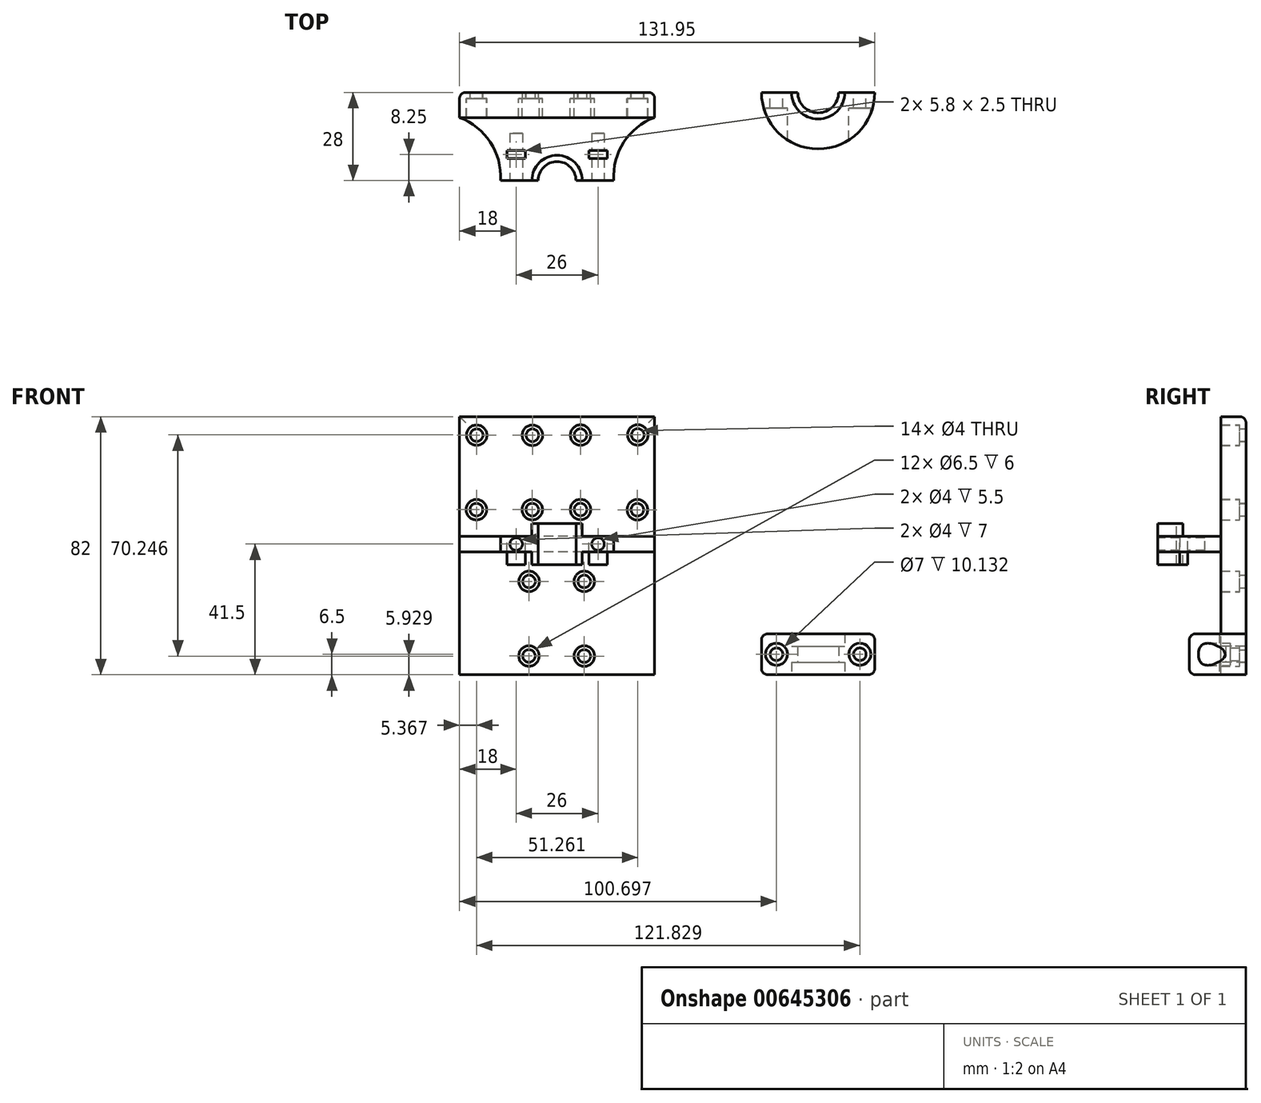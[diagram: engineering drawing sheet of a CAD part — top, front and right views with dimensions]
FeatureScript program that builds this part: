
annotation { "Feature Type Name" : "Feature", "Feature Type Description" : "" }
export const myFeature = defineFeature(function(context is Context, id is Id, definition is map)
    precondition{}
    {
        {
            var Q0;
            Q0=qCreatedBy(makeId("Front.planeOp"),FACE);
            var sketch = newSketch(context, id + "F0", { "sketchPlane" : qUnion([Q0])});
            skLineSegment(sketch, "E0.bottom", {"start": v(0, 0) * mm, "end": v(-62, 0) * mm});
            skLineSegment(sketch, "E0.top", {"start": v(0, 82) * mm, "end": v(-62, 82) * mm});
            skLineSegment(sketch, "E0.left", {"start": v(0, 0) * mm, "end": v(0, 82) * mm});
            skLineSegment(sketch, "E0.right", {"start": v(-62, 0) * mm, "end": v(-62, 82) * mm});
            skLineSegment(sketch, "E1.bottom", {"start": v(-62, 82) * mm, "end": v(-32, 82) * mm});
            skLineSegment(sketch, "E1.top", {"start": v(-62, 48) * mm, "end": v(-32, 48) * mm});
            skLineSegment(sketch, "E1.left", {"start": v(-62, 82) * mm, "end": v(-62, 48) * mm});
            skLineSegment(sketch, "E1.right", {"start": v(-32, 82) * mm, "end": v(-32, 48) * mm});
            skLineSegment(sketch, "E2.bottom", {"start": v(0, 82) * mm, "end": v(-30, 82) * mm});
            skLineSegment(sketch, "E2.top", {"start": v(0, 48) * mm, "end": v(-30, 48) * mm});
            skLineSegment(sketch, "E2.left", {"start": v(0, 82) * mm, "end": v(0, 48) * mm});
            skLineSegment(sketch, "E2.right", {"start": v(-30, 82) * mm, "end": v(-30, 48) * mm});
            skLineSegment(sketch, "E3", {"start": v(-62, 0) * mm, "end": v(-46, 0) * mm});
            skLineSegment(sketch, "E4.bottom", {"start": v(-46, 0) * mm, "end": v(-16, 0) * mm});
            skLineSegment(sketch, "E4.top", {"start": v(-46, 34) * mm, "end": v(-16, 34) * mm});
            skLineSegment(sketch, "E4.left", {"start": v(-46, 0) * mm, "end": v(-46, 34) * mm});
            skLineSegment(sketch, "E4.right", {"start": v(-16, 0) * mm, "end": v(-16, 34) * mm});
            skLineSegment(sketch, "E5", {"start": v(-62, 82) * mm, "end": v(-58.7, 82) * mm});
            skLineSegment(sketch, "E6", {"start": v(-58.7, 82) * mm, "end": v(-36.7, 82) * mm});
            skLineSegment(sketch, "E7", {"start": v(0, 82) * mm, "end": v(-3.3, 82) * mm});
            skLineSegment(sketch, "E8", {"start": v(-3.3, 82) * mm, "end": v(-25.3, 82) * mm});
            skLineSegment(sketch, "E9", {"start": v(0, 82) * mm, "end": v(0, 78.3) * mm});
            skLineSegment(sketch, "E10", {"start": v(0, 78.3) * mm, "end": v(0, 50.3) * mm});
            skLineSegment(sketch, "E11", {"start": v(-58.7, 82) * mm, "end": v(-58.7, 48) * mm, "construction": true});
            skLineSegment(sketch, "E12", {"start": v(-36.7, 82) * mm, "end": v(-36.7, 48) * mm, "construction": true});
            skLineSegment(sketch, "E13", {"start": v(-25.3, 82) * mm, "end": v(-25.3, 48) * mm, "construction": true});
            skLineSegment(sketch, "E14", {"start": v(-3.3, 82) * mm, "end": v(-3.3, 48) * mm, "construction": true});
            skLineSegment(sketch, "E15", {"start": v(0, 78.3) * mm, "end": v(-58.7, 78.3) * mm, "construction": true});
            skLineSegment(sketch, "E16", {"start": v(0, 50.3) * mm, "end": v(-58.7, 50.3) * mm, "construction": true});
            skLineSegment(sketch, "E17", {"start": v(-62, 0) * mm, "end": v(-42, 0) * mm});
            skLineSegment(sketch, "E18", {"start": v(-42, 0) * mm, "end": v(-20.3, 0) * mm});
            skLineSegment(sketch, "E19", {"start": v(-20.3, 0) * mm, "end": v(0, 0) * mm});
            skLineSegment(sketch, "E20", {"start": v(-42, 0) * mm, "end": v(-42, 34) * mm, "construction": true});
            skLineSegment(sketch, "E21", {"start": v(-20.3, 0) * mm, "end": v(-20.3, 34) * mm, "construction": true});
            skLineSegment(sketch, "E22", {"start": v(-16, 0) * mm, "end": v(-16, 3.9) * mm});
            skLineSegment(sketch, "E23", {"start": v(-16, 3.9) * mm, "end": v(-16, 31.7) * mm});
            skLineSegment(sketch, "E24", {"start": v(-16, 31.7) * mm, "end": v(-42, 31.7) * mm, "construction": true});
            skLineSegment(sketch, "E25", {"start": v(-16, 3.9) * mm, "end": v(-42, 3.9) * mm, "construction": true});
            skCircle(sketch, "E26", {"center": v(-39.91, 29.63) * mm, "radius": 2 * mm});
            skCircle(sketch, "E27", {"center": v(-22.37, 29.64) * mm, "radius": 2 * mm});
            skCircle(sketch, "E28", {"center": v(-22.36, 5.93) * mm, "radius": 2 * mm});
            skCircle(sketch, "E29", {"center": v(-39.93, 5.95) * mm, "radius": 2 * mm});
            skCircle(sketch, "E30", {"center": v(-39.91, 29.63) * mm, "radius": 3.25 * mm});
            skCircle(sketch, "E31", {"center": v(-22.37, 29.64) * mm, "radius": 3.25 * mm});
            skCircle(sketch, "E32", {"center": v(-39.93, 5.95) * mm, "radius": 3.25 * mm});
            skCircle(sketch, "E33", {"center": v(-22.36, 5.93) * mm, "radius": 3.25 * mm});
            skCircle(sketch, "E34", {"center": v(-56.63, 52.43) * mm, "radius": 2 * mm});
            skCircle(sketch, "E35", {"center": v(-38.89, 52.44) * mm, "radius": 2 * mm});
            skCircle(sketch, "E36", {"center": v(-56.55, 76.1) * mm, "radius": 2 * mm});
            skCircle(sketch, "E37", {"center": v(-38.84, 76.08) * mm, "radius": 2 * mm});
            skCircle(sketch, "E38", {"center": v(-23.55, 76.11) * mm, "radius": 2 * mm});
            skCircle(sketch, "E39", {"center": v(-5.37, 76.17) * mm, "radius": 2 * mm});
            skCircle(sketch, "E40", {"center": v(-5.5, 52.4) * mm, "radius": 2 * mm});
            skCircle(sketch, "E41", {"center": v(-23.55, 52.48) * mm, "radius": 2 * mm});
            skCircle(sketch, "E42", {"center": v(-56.55, 76.1) * mm, "radius": 3.25 * mm});
            skCircle(sketch, "E43", {"center": v(-38.84, 76.08) * mm, "radius": 3.25 * mm});
            skCircle(sketch, "E44", {"center": v(-56.63, 52.43) * mm, "radius": 3.25 * mm});
            skCircle(sketch, "E45", {"center": v(-38.89, 52.44) * mm, "radius": 3.25 * mm});
            skCircle(sketch, "E46", {"center": v(-23.55, 52.48) * mm, "radius": 3.25 * mm});
            skCircle(sketch, "E47", {"center": v(-5.5, 52.4) * mm, "radius": 3.25 * mm});
            skCircle(sketch, "E48", {"center": v(-23.55, 76.11) * mm, "radius": 3.25 * mm});
            skCircle(sketch, "E49", {"center": v(-5.37, 76.17) * mm, "radius": 3.25 * mm});
            skSolve(sketch);
        }
        {
            var Q0;
            Q0 = qSketchRegion(id + "F0", true);
            extrude(context, id + "F1", {"entities" : qUnion([Q0]), "depth" : 8 * mm, "offsetDistance" : 25 * mm});
        }
        {
            var Q0;
            Q0=makeQuery(id+"F0.imprint","IMPRINT",FACE,{"disambiguationData":[TD([[makeQuery(id+"F0.imprint","IMPRINT",EDGE,{"derivedFrom":sQuery(id+"F0.wireOp",EDGE,"E36")}),-1.0]])]});
            var Q1;
            Q1=makeQuery(id+"F0.imprint","IMPRINT",FACE,{"disambiguationData":[TD([[makeQuery(id+"F0.imprint","IMPRINT",EDGE,{"derivedFrom":sQuery(id+"F0.wireOp",EDGE,"E37")}),-1.0]])]});
            var Q2;
            Q2=makeQuery(id+"F0.imprint","IMPRINT",FACE,{"disambiguationData":[TD([[makeQuery(id+"F0.imprint","IMPRINT",EDGE,{"derivedFrom":sQuery(id+"F0.wireOp",EDGE,"E38")}),-1.0]])]});
            var Q3;
            Q3=makeQuery(id+"F0.imprint","IMPRINT",FACE,{"disambiguationData":[TD([[makeQuery(id+"F0.imprint","IMPRINT",EDGE,{"derivedFrom":sQuery(id+"F0.wireOp",EDGE,"E39")}),-1.0]])]});
            var Q4;
            Q4=makeQuery(id+"F0.imprint","IMPRINT",FACE,{"disambiguationData":[TD([[makeQuery(id+"F0.imprint","IMPRINT",EDGE,{"derivedFrom":sQuery(id+"F0.wireOp",EDGE,"E40")}),-1.0]])]});
            var Q5;
            Q5=makeQuery(id+"F0.imprint","IMPRINT",FACE,{"disambiguationData":[TD([[makeQuery(id+"F0.imprint","IMPRINT",EDGE,{"derivedFrom":sQuery(id+"F0.wireOp",EDGE,"E41")}),-1.0]])]});
            var Q6;
            Q6=makeQuery(id+"F0.imprint","IMPRINT",FACE,{"disambiguationData":[TD([[makeQuery(id+"F0.imprint","IMPRINT",EDGE,{"derivedFrom":sQuery(id+"F0.wireOp",EDGE,"E35")}),-1.0]])]});
            var Q7;
            Q7=makeQuery(id+"F0.imprint","IMPRINT",FACE,{"disambiguationData":[TD([[makeQuery(id+"F0.imprint","IMPRINT",EDGE,{"derivedFrom":sQuery(id+"F0.wireOp",EDGE,"E34")}),-1.0]])]});
            var Q8;
            Q8=makeQuery(id+"F0.imprint","IMPRINT",FACE,{"disambiguationData":[TD([[makeQuery(id+"F0.imprint","IMPRINT",EDGE,{"derivedFrom":sQuery(id+"F0.wireOp",EDGE,"E26")}),-1.0]])]});
            var Q9;
            Q9=makeQuery(id+"F0.imprint","IMPRINT",FACE,{"disambiguationData":[TD([[makeQuery(id+"F0.imprint","IMPRINT",EDGE,{"derivedFrom":sQuery(id+"F0.wireOp",EDGE,"E27")}),-1.0]])]});
            var Q10;
            Q10=makeQuery(id+"F0.imprint","IMPRINT",FACE,{"disambiguationData":[TD([[makeQuery(id+"F0.imprint","IMPRINT",EDGE,{"derivedFrom":sQuery(id+"F0.wireOp",EDGE,"E28")}),-1.0]])]});
            var Q11;
            Q11=makeQuery(id+"F0.imprint","IMPRINT",FACE,{"disambiguationData":[TD([[makeQuery(id+"F0.imprint","IMPRINT",EDGE,{"derivedFrom":sQuery(id+"F0.wireOp",EDGE,"E29")}),-1.0]])]});
            extrude(context, id + "F2", {"entities" : qUnion([Q0, Q1, Q2, Q3, Q4, Q5, Q6, Q7, Q8, Q9, Q10, Q11]), "operationType" : NewBodyOperationType.ADD, "depth" : 2 * mm, "offsetDistance" : 25 * mm});
        }
        {
            var Q0;
            Q0=makeQuery(id+"F1.opExtrude","CAP_FACE",FACE,{"disambiguationData":[OSD([sQuery(id+"F0.wireOp",EDGE,"E0.top"),sQuery(id+"F0.wireOp",EDGE,"E0.left"),sQuery(id+"F0.wireOp",EDGE,"E0.right"),sQuery(id+"F0.wireOp",EDGE,"E1.bottom"),sQuery(id+"F0.wireOp",EDGE,"E1.left"),sQuery(id+"F0.wireOp",EDGE,"E2.bottom"),sQuery(id+"F0.wireOp",EDGE,"E2.left"),sQuery(id+"F0.wireOp",EDGE,"E5"),sQuery(id+"F0.wireOp",EDGE,"E6"),sQuery(id+"F0.wireOp",EDGE,"E7"),sQuery(id+"F0.wireOp",EDGE,"E8"),sQuery(id+"F0.wireOp",EDGE,"E9"),sQuery(id+"F0.wireOp",EDGE,"E10"),sQuery(id+"F0.wireOp",EDGE,"E17"),sQuery(id+"F0.wireOp",EDGE,"E18"),sQuery(id+"F0.wireOp",EDGE,"E19"),sQuery(id+"F0.wireOp",EDGE,"E30"),sQuery(id+"F0.wireOp",EDGE,"E31"),sQuery(id+"F0.wireOp",EDGE,"E32"),sQuery(id+"F0.wireOp",EDGE,"E33"),sQuery(id+"F0.wireOp",EDGE,"E42"),sQuery(id+"F0.wireOp",EDGE,"E43"),sQuery(id+"F0.wireOp",EDGE,"E44"),sQuery(id+"F0.wireOp",EDGE,"E45"),sQuery(id+"F0.wireOp",EDGE,"E46"),sQuery(id+"F0.wireOp",EDGE,"E47"),sQuery(id+"F0.wireOp",EDGE,"E48"),sQuery(id+"F0.wireOp",EDGE,"E49")])],"isStart":false});
            var sketch = newSketch(context, id + "F3", { "sketchPlane" : qUnion([Q0])});
            skLineSegment(sketch, "E50", {"start": v(0, 0) * mm, "end": v(0, 48) * mm});
            skLineSegment(sketch, "E51", {"start": v(0, 48) * mm, "end": v(-62, 48) * mm});
            skLineSegment(sketch, "E52", {"start": v(0, 48) * mm, "end": v(0, 35) * mm});
            skLineSegment(sketch, "E53", {"start": v(0, 35) * mm, "end": v(-62, 35) * mm});
            skLineSegment(sketch, "E54", {"start": v(-62, 35) * mm, "end": v(-62, 48) * mm});
            skSolve(sketch);
        }
        {
            var Q0;
            Q0 = qSketchRegion(id + "F3", true);
            extrude(context, id + "F4", {"entities" : qUnion([Q0]), "operationType" : NewBodyOperationType.ADD, "depth" : 20 * mm, "offsetDistance" : 25 * mm});
        }
        {
            var Q0;
            Q0=makeQuery(id+"F4.opExtrude","SWEPT_FACE",FACE,{"disambiguationData":[OSD([sQuery(id+"F3.wireOp",EDGE,"E51")])]});
            var sketch = newSketch(context, id + "F5", { "sketchPlane" : qUnion([Q0])});
            skLineSegment(sketch, "E55", {"start": v(-62, -28) * mm, "end": v(-39, -28) * mm});
            skLineSegment(sketch, "E56", {"start": v(-39, -28) * mm, "end": v(-23, -28) * mm});
            skLineSegment(sketch, "E57", {"start": v(-39, -28) * mm, "end": v(-49, -28) * mm});
            skLineSegment(sketch, "E58", {"start": v(-23, -28) * mm, "end": v(-13, -28) * mm});
            skArc(sketch, "E59", {"start": v(-49, -28) * mm, "mid": v(-52.2, -15.85) * mm, "end": v(-62, -8) * mm});
            skArc(sketch, "E60", {"start": v(0, -8) * mm, "mid": v(-9.8, -15.85) * mm, "end": v(-13, -28) * mm});
            skArc(sketch, "E61", {"start": v(-39, -28) * mm, "mid": v(-31, -20) * mm, "end": v(-23, -28) * mm});
            skArc(sketch, "E62", {"start": v(-25, -28) * mm, "mid": v(-31, -22) * mm, "end": v(-37, -28) * mm});
            skLineSegment(sketch, "E63", {"start": v(-49, -28) * mm, "end": v(-46.9, -28) * mm});
            skLineSegment(sketch, "E64", {"start": v(-46.9, -21) * mm, "end": v(-46.9, -18.5) * mm});
            skLineSegment(sketch, "E65", {"start": v(-46.9, -18.5) * mm, "end": v(-41.1, -18.5) * mm});
            skLineSegment(sketch, "E66", {"start": v(-41.1, -18.5) * mm, "end": v(-41.1, -21) * mm});
            skLineSegment(sketch, "E67", {"start": v(-41.1, -21) * mm, "end": v(-46.9, -21) * mm});
            skLineSegment(sketch, "E68", {"start": v(-31, -28) * mm, "end": v(-31, -15.15) * mm, "construction": true});
            skLineSegment(sketch, "E69.MirrorCS", {"start": v(-20.9, -18.5) * mm, "end": v(-20.9, -21) * mm});
            skLineSegment(sketch, "E70.MirrorCS", {"start": v(-15.1, -18.5) * mm, "end": v(-20.9, -18.5) * mm});
            skLineSegment(sketch, "E71.MirrorCS", {"start": v(-15.1, -21) * mm, "end": v(-15.1, -18.5) * mm});
            skLineSegment(sketch, "E72.MirrorCS", {"start": v(-20.9, -21) * mm, "end": v(-15.1, -21) * mm});
            skSolve(sketch);
        }
        {
            var Q0;
            Q0=makeQuery(id+"F5.imprint","IMPRINT",FACE,{"disambiguationData":[TD([[makeQuery(id+"F5.imprint","IMPRINT",EDGE,{"derivedFrom":sQuery(id+"F5.wireOp",EDGE,"E55")}),-1.0]])]});
            var Q1;
            {var subQ0=sQuery(id+"F5.wireOp",EDGE,"E60");Q1=makeQuery(id+"F5.imprint","IMPRINT",FACE,{"disambiguationData":[TD([[makeQuery(id+"F5.imprint","IMPRINT",EDGE,{"derivedFrom":subQ0}),1.0]])]});}
            extrude(context, id + "F6", {"entities" : qUnion([Q0, Q1]), "operationType" : NewBodyOperationType.REMOVE, "oppositeDirection" : true, "depth" : 25 * mm, "offsetDistance" : 25 * mm});
        }
        {
            var Q0;
            Q0=makeQuery(id+"F5.imprint","IMPRINT",FACE,{"disambiguationData":[TD([[makeQuery(id+"F5.imprint","IMPRINT",EDGE,{"derivedFrom":sQuery(id+"F5.wireOp",EDGE,"E65")}),-1.0]])]});
            var Q1;
            Q1=makeQuery(id+"F5.imprint","IMPRINT",FACE,{"disambiguationData":[TD([[makeQuery(id+"F5.imprint","IMPRINT",EDGE,{"derivedFrom":sQuery(id+"F5.wireOp",EDGE,"66e045d4-452c-4d9e-82fe-42991698a6ae0.MirrorCS")}),1.0]])]});
            extrude(context, id + "F7", {"entities" : qUnion([Q0, Q1]), "operationType" : NewBodyOperationType.REMOVE, "oppositeDirection" : true, "depth" : 9 * mm, "offsetDistance" : 25 * mm});
        }
        {
            var Q0;
            {var subQ0=sQuery(id+"F5.wireOp",EDGE,"E62");Q0=makeQuery(id+"F5.imprint","IMPRINT",FACE,{"disambiguationData":[TD([[makeQuery(id+"F5.imprint","IMPRINT",EDGE,{"derivedFrom":subQ0}),1.0]])]});}
            var Q1;
            {var subQ0=sQuery(id+"F5.wireOp",EDGE,"E61");Q1=makeQuery(id+"F5.imprint","IMPRINT",FACE,{"disambiguationData":[TD([[makeQuery(id+"F5.imprint","IMPRINT",EDGE,{"derivedFrom":subQ0}),-1.0]])]});}
            extrude(context, id + "F8", {"entities" : qUnion([Q0, Q1]), "operationType" : NewBodyOperationType.REMOVE, "oppositeDirection" : true, "depth" : 25 * mm, "offsetDistance" : 25 * mm});
        }
        {
            var Q0;
            {var subQ0=sQuery(id+"F5.wireOp",EDGE,"E61");Q0=makeQuery(id+"F5.imprint","IMPRINT",FACE,{"disambiguationData":[TD([[makeQuery(id+"F5.imprint","IMPRINT",EDGE,{"derivedFrom":subQ0}),-1.0]])]});}
            extrude(context, id + "F9", {"entities" : qUnion([Q0]), "operationType" : NewBodyOperationType.ADD, "oppositeDirection" : true, "depth" : 9 * mm, "offsetDistance" : 25 * mm});
        }
        {
            var Q0;
            {var subQ0=sQuery(id+"F5.wireOp",EDGE,"E61");Q0=makeQuery(id+"F5.imprint","IMPRINT",FACE,{"disambiguationData":[TD([[makeQuery(id+"F5.imprint","IMPRINT",EDGE,{"derivedFrom":subQ0}),-1.0]])]});}
            extrude(context, id + "F10", {"entities" : qUnion([Q0]), "operationType" : NewBodyOperationType.REMOVE, "oppositeDirection" : true, "depth" : 4 * mm, "offsetDistance" : 25 * mm});
        }
        {
            var Q0;
            {var subQ1=sQuery(id+"F5.wireOp",EDGE,"E56");var subQ2=sQuery(id+"F3.wireOp",EDGE,"E51");var subQ3=sQuery(id+"F3.wireOp",EDGE,"E53");Q0=makeQuery(id+"F9.boolean.opBoolean","MERGE",FACE,{"derivedFrom":[makeQuery(id+"F8.boolean.opBoolean","SPLIT",FACE,{"disambiguationData":[TD([makeQuery(id+"F6.boolean.opBoolean","COPY",FACE,{"derivedFrom":makeQuery(id+"F6.opExtrude","SWEPT_FACE",FACE,{"disambiguationData":[OSD([sQuery(id+"F5.wireOp",EDGE,"E59")])]})})])],"derivedFrom":makeQuery(id+"F4.opExtrude","CAP_FACE",FACE,{"disambiguationData":[OSD([subQ2,sQuery(id+"F3.wireOp",EDGE,"E52"),subQ3,sQuery(id+"F3.wireOp",EDGE,"E54")])],"isStart":false})}),makeQuery(id+"F9.opExtrude","SWEPT_FACE",FACE,{"disambiguationData":[OSD([subQ1]),TDD([makeQuery(id+"F5.imprint","IMPRINT",EDGE,{"disambiguationData":[TD([[makeQuery(id+"F5.imprint","INTERSECT",VERTEX,{"disambiguationData":[OD(1.0)],"derivedFrom":[subQ1,sQuery(id+"F5.wireOp",EDGE,"E62")]}),-1.0]])],"derivedFrom":subQ1})])]})]});}
            var sketch = newSketch(context, id + "F11", { "sketchPlane" : qUnion([Q0])});
            skLineSegment(sketch, "E73", {"start": v(-49, 48) * mm, "end": v(-44, 48) * mm});
            skLineSegment(sketch, "E74", {"start": v(-44, 48) * mm, "end": v(-44, 41.5) * mm});
            skPoint(sketch, "E74.endSnap0", {"position": v(-49, 41.5) * mm});
            skCircle(sketch, "E75", {"center": v(-44, 41.5) * mm, "radius": 2 * mm});
            skSolve(sketch);
        }
        {
            var Q0;
            Q0 = qSketchRegion(id + "F11", true);
            extrude(context, id + "F12", {"entities" : qUnion([Q0]), "operationType" : NewBodyOperationType.REMOVE, "oppositeDirection" : true, "depth" : 15 * mm, "offsetDistance" : 25 * mm});
        }
        {
            var Q0;
            {var subQ1=sQuery(id+"F5.wireOp",EDGE,"E56");var subQ2=sQuery(id+"F3.wireOp",EDGE,"E51");var subQ3=sQuery(id+"F3.wireOp",EDGE,"E53");Q0=makeQuery(id+"F9.boolean.opBoolean","MERGE",FACE,{"derivedFrom":[makeQuery(id+"F8.boolean.opBoolean","SPLIT",FACE,{"disambiguationData":[TD([makeQuery(id+"F6.boolean.opBoolean","COPY",FACE,{"derivedFrom":makeQuery(id+"F6.opExtrude","SWEPT_FACE",FACE,{"disambiguationData":[OSD([sQuery(id+"F5.wireOp",EDGE,"E60")])]})})])],"derivedFrom":makeQuery(id+"F4.opExtrude","CAP_FACE",FACE,{"disambiguationData":[OSD([subQ2,sQuery(id+"F3.wireOp",EDGE,"E52"),subQ3,sQuery(id+"F3.wireOp",EDGE,"E54")])],"isStart":false})}),makeQuery(id+"F9.opExtrude","SWEPT_FACE",FACE,{"disambiguationData":[OSD([subQ1]),TDD([makeQuery(id+"F5.imprint","IMPRINT",EDGE,{"disambiguationData":[TD([[makeQuery(id+"F5.imprint","INTERSECT",VERTEX,{"disambiguationData":[OD(0.0)],"derivedFrom":[subQ1,sQuery(id+"F5.wireOp",EDGE,"E62")]}),1.0]])],"derivedFrom":subQ1})])]})]});}
            var sketch = newSketch(context, id + "F13", { "sketchPlane" : qUnion([Q0])});
            skLineSegment(sketch, "E76", {"start": v(-13, 48) * mm, "end": v(-18, 48) * mm});
            skLineSegment(sketch, "E77", {"start": v(-18, 48) * mm, "end": v(-18, 41.5) * mm});
            skPoint(sketch, "E77.endSnap0", {"position": v(-13, 41.5) * mm});
            skCircle(sketch, "E78", {"center": v(-18, 41.5) * mm, "radius": 2 * mm});
            skSolve(sketch);
        }
        {
            var Q0;
            Q0 = qSketchRegion(id + "F13", true);
            extrude(context, id + "F14", {"entities" : qUnion([Q0]), "operationType" : NewBodyOperationType.REMOVE, "oppositeDirection" : true, "depth" : 15 * mm, "offsetDistance" : 25 * mm});
        }
        {
            var Q0;
            Q0=makeQuery(id+"F1.opExtrude","CAP_EDGE",EDGE,{"disambiguationData":[OSD([sQuery(id+"F0.wireOp",EDGE,"E0.top"),sQuery(id+"F0.wireOp",EDGE,"E1.bottom"),sQuery(id+"F0.wireOp",EDGE,"E2.bottom"),sQuery(id+"F0.wireOp",EDGE,"E5"),sQuery(id+"F0.wireOp",EDGE,"E6"),sQuery(id+"F0.wireOp",EDGE,"E7"),sQuery(id+"F0.wireOp",EDGE,"E8")])],"isStart":true});
            var Q1;
            Q1=makeQuery(id+"F1.opExtrude","CAP_EDGE",EDGE,{"disambiguationData":[OSD([sQuery(id+"F0.wireOp",EDGE,"E0.right"),sQuery(id+"F0.wireOp",EDGE,"E1.left")])],"isStart":true});
            var Q2;
            Q2=makeQuery(id+"F1.opExtrude","CAP_EDGE",EDGE,{"disambiguationData":[OSD([sQuery(id+"F0.wireOp",EDGE,"E0.left"),sQuery(id+"F0.wireOp",EDGE,"E2.left"),sQuery(id+"F0.wireOp",EDGE,"E9"),sQuery(id+"F0.wireOp",EDGE,"E10")])],"isStart":true});
            var Q3;
            Q3=makeQuery(id+"F1.opExtrude","CAP_EDGE",EDGE,{"disambiguationData":[OSD([sQuery(id+"F0.wireOp",EDGE,"E17"),sQuery(id+"F0.wireOp",EDGE,"E18"),sQuery(id+"F0.wireOp",EDGE,"E19")])],"isStart":true});
            var Q4;
            Q4=makeQuery(id+"F6.boolean.opBoolean","COPY",EDGE,{"derivedFrom":makeQuery(id+"F6.opExtrude","CAP_EDGE",EDGE,{"disambiguationData":[OSD([sQuery(id+"F5.wireOp",EDGE,"E60")])],"isStart":true})});
            var Q5;
            Q5=makeQuery(id+"F6.boolean.opBoolean","INTERSECT",EDGE,{"derivedFrom":[makeQuery(id+"F4.opExtrude","SWEPT_FACE",FACE,{"disambiguationData":[OSD([sQuery(id+"F3.wireOp",EDGE,"E53")])]}),makeQuery(id+"F6.opExtrude","SWEPT_FACE",FACE,{"disambiguationData":[OSD([sQuery(id+"F5.wireOp",EDGE,"E60")])]})]});
            var Q6;
            Q6=makeQuery(id+"F6.boolean.opBoolean","COPY",EDGE,{"derivedFrom":makeQuery(id+"F6.opExtrude","CAP_EDGE",EDGE,{"disambiguationData":[OSD([sQuery(id+"F5.wireOp",EDGE,"E59")])],"isStart":true})});
            var Q7;
            Q7=makeQuery(id+"F6.boolean.opBoolean","INTERSECT",EDGE,{"derivedFrom":[makeQuery(id+"F4.opExtrude","SWEPT_FACE",FACE,{"disambiguationData":[OSD([sQuery(id+"F3.wireOp",EDGE,"E53")])]}),makeQuery(id+"F6.opExtrude","SWEPT_FACE",FACE,{"disambiguationData":[OSD([sQuery(id+"F5.wireOp",EDGE,"E59")])]})]});
            fillet(context, id + "F15", {"entities" : qUnion([Q0, Q1, Q2, Q3, Q4, Q5, Q6, Q7]), "radius" : 2 * mm, "tangentPropagation" : true, "allowEdgeOverflow" : false});
        }
        {
            var Q0;
            Q0=qCreatedBy(makeId("Top.planeOp"),FACE);
            var sketch = newSketch(context, id + "F16", { "sketchPlane" : qUnion([Q0])});
            skLineSegment(sketch, "E79.bottom", {"start": v(33.95, 0) * mm, "end": v(69.95, 0) * mm});
            skLineSegment(sketch, "E79.top", {"start": v(33.95, -20) * mm, "end": v(69.95, -20) * mm});
            skLineSegment(sketch, "E79.left", {"start": v(33.95, 0) * mm, "end": v(33.95, -20) * mm});
            skLineSegment(sketch, "E79.right", {"start": v(69.95, 0) * mm, "end": v(69.95, -20) * mm});
            skArc(sketch, "E80", {"start": v(33.95, 0) * mm, "mid": v(51.95, -18) * mm, "end": v(69.95, 0) * mm});
            skArc(sketch, "E81", {"start": v(43.45, 0) * mm, "mid": v(51.95, -8.5) * mm, "end": v(60.45, 0) * mm});
            skArc(sketch, "E82", {"start": v(45.45, 0) * mm, "mid": v(51.95, -6.5) * mm, "end": v(58.45, 0) * mm});
            skLineSegment(sketch, "E83", {"start": v(33.95, -18.5) * mm, "end": v(69.95, -18.5) * mm});
            skLineSegment(sketch, "E84", {"start": v(69.95, -18.5) * mm, "end": v(70.2, -17.78) * mm});
            skSolve(sketch);
        }
        {
            var Q0;
            {var subQ5=sQuery(id+"F16.wireOp",EDGE,"E81");Q0=makeQuery(id+"F16.imprint","IMPRINT",FACE,{"disambiguationData":[TD([[makeQuery(id+"F16.imprint","IMPRINT",EDGE,{"derivedFrom":subQ5}),-1.0]])]});}
            extrude(context, id + "F17", {"entities" : qUnion([Q0]), "depth" : 13 * mm, "offsetDistance" : 25 * mm});
        }
        {
            var Q0;
            {var subQ0=sQuery(id+"F16.wireOp",EDGE,"E81");Q0=makeQuery(id+"F16.imprint","IMPRINT",FACE,{"disambiguationData":[TD([[makeQuery(id+"F16.imprint","IMPRINT",EDGE,{"derivedFrom":subQ0}),1.0]])]});}
            extrude(context, id + "F18", {"entities" : qUnion([Q0]), "operationType" : NewBodyOperationType.ADD, "depth" : 9 * mm, "offsetDistance" : 25 * mm});
        }
        {
            var Q0;
            {var subQ0=sQuery(id+"F16.wireOp",EDGE,"E81");Q0=makeQuery(id+"F16.imprint","IMPRINT",FACE,{"disambiguationData":[TD([[makeQuery(id+"F16.imprint","IMPRINT",EDGE,{"derivedFrom":subQ0}),1.0]])]});}
            extrude(context, id + "F19", {"entities" : qUnion([Q0]), "operationType" : NewBodyOperationType.REMOVE, "depth" : 4 * mm, "offsetDistance" : 25 * mm});
        }
        {
            var Q0;
            {var subQ0=sQuery(id+"F16.wireOp",EDGE,"E79.bottom");var subQ1=makeQuery(id+"F16.imprint","INTERSECT",VERTEX,{"disambiguationData":[OD(1.0)],"derivedFrom":[subQ0,sQuery(id+"F16.wireOp",EDGE,"E81")]});Q0=makeQuery(id+"F18.boolean.opBoolean","MERGE",FACE,{"derivedFrom":[makeQuery(id+"F17.opExtrude","SWEPT_FACE",FACE,{"disambiguationData":[OSD([subQ0]),TDD([makeQuery(id+"F16.imprint","IMPRINT",EDGE,{"disambiguationData":[TD([[subQ1,-1.0]])],"derivedFrom":subQ0})])]}),makeQuery(id+"F18.opExtrude","SWEPT_FACE",FACE,{"disambiguationData":[OSD([subQ0]),TDD([makeQuery(id+"F16.imprint","IMPRINT",EDGE,{"disambiguationData":[TD([[subQ1,1.0]])],"derivedFrom":subQ0})])]})]});}
            var sketch = newSketch(context, id + "F20", { "sketchPlane" : qUnion([Q0])});
            skLineSegment(sketch, "E85", {"start": v(-69.95, 13) * mm, "end": v(-65.2, 13) * mm});
            skLineSegment(sketch, "E86", {"start": v(-65.2, 13) * mm, "end": v(-65.2, 6.5) * mm});
            skPoint(sketch, "E86.endSnap0", {"position": v(-69.95, 6.5) * mm});
            skCircle(sketch, "E87", {"center": v(-65.2, 6.5) * mm, "radius": 2 * mm});
            skCircle(sketch, "E88", {"center": v(-65.2, 6.5) * mm, "radius": 3.5 * mm});
            skSolve(sketch);
        }
        {
            var Q0;
            Q0 = qSketchRegion(id + "F20", true);
            var Q1;
            Q1=makeQuery(id+"F20.imprint","IMPRINT",FACE,{"disambiguationData":[TD([[makeQuery(id+"F20.imprint","IMPRINT",EDGE,{"derivedFrom":sQuery(id+"F20.wireOp",EDGE,"E87")}),1.0]])]});
            extrude(context, id + "F21", {"entities" : qUnion([Q0, Q1]), "operationType" : NewBodyOperationType.REMOVE, "oppositeDirection" : true, "depth" : 25 * mm, "offsetDistance" : 25 * mm});
        }
        {
            var Q0;
            Q0=makeQuery(id+"F20.imprint","IMPRINT",FACE,{"disambiguationData":[TD([[makeQuery(id+"F20.imprint","IMPRINT",EDGE,{"derivedFrom":sQuery(id+"F20.wireOp",EDGE,"E87")}),-1.0]])]});
            extrude(context, id + "F22", {"entities" : qUnion([Q0]), "operationType" : NewBodyOperationType.ADD, "oppositeDirection" : true, "depth" : 5 * mm, "offsetDistance" : 25 * mm});
        }
        {
            var Q0;
            {var subQ0=sQuery(id+"F16.wireOp",EDGE,"E79.bottom");var subQ1=makeQuery(id+"F16.imprint","INTERSECT",VERTEX,{"disambiguationData":[OD(0.0)],"derivedFrom":[subQ0,sQuery(id+"F16.wireOp",EDGE,"E81")]});Q0=makeQuery(id+"F18.boolean.opBoolean","MERGE",FACE,{"derivedFrom":[makeQuery(id+"F17.opExtrude","SWEPT_FACE",FACE,{"disambiguationData":[OSD([subQ0]),TDD([makeQuery(id+"F16.imprint","IMPRINT",EDGE,{"disambiguationData":[TD([[subQ1,1.0]])],"derivedFrom":subQ0})])]}),makeQuery(id+"F18.opExtrude","SWEPT_FACE",FACE,{"disambiguationData":[OSD([subQ0]),TDD([makeQuery(id+"F16.imprint","IMPRINT",EDGE,{"disambiguationData":[TD([[subQ1,-1.0]])],"derivedFrom":subQ0})])]})]});}
            var sketch = newSketch(context, id + "F23", { "sketchPlane" : qUnion([Q0])});
            skLineSegment(sketch, "E89", {"start": v(-33.95, 13) * mm, "end": v(-38.7, 13) * mm});
            skLineSegment(sketch, "E90", {"start": v(-38.7, 13) * mm, "end": v(-38.7, 6.5) * mm});
            skPoint(sketch, "E90.endSnap0", {"position": v(-33.95, 6.5) * mm});
            skCircle(sketch, "E91", {"center": v(-38.7, 6.5) * mm, "radius": 2 * mm});
            skCircle(sketch, "E92", {"center": v(-38.7, 6.5) * mm, "radius": 3.5 * mm});
            skSolve(sketch);
        }
        {
            var Q0;
            Q0=makeQuery(id+"F23.imprint","IMPRINT",FACE,{"disambiguationData":[TD([[makeQuery(id+"F23.imprint","IMPRINT",EDGE,{"derivedFrom":sQuery(id+"F23.wireOp",EDGE,"E91")}),1.0]])]});
            var Q1;
            Q1=makeQuery(id+"F23.imprint","IMPRINT",FACE,{"disambiguationData":[TD([[makeQuery(id+"F23.imprint","IMPRINT",EDGE,{"derivedFrom":sQuery(id+"F23.wireOp",EDGE,"E91")}),-1.0]])]});
            extrude(context, id + "F24", {"entities" : qUnion([Q0, Q1]), "operationType" : NewBodyOperationType.REMOVE, "oppositeDirection" : true, "depth" : 25 * mm, "offsetDistance" : 25 * mm});
        }
        {
            var Q0;
            Q0=makeQuery(id+"F23.imprint","IMPRINT",FACE,{"disambiguationData":[TD([[makeQuery(id+"F23.imprint","IMPRINT",EDGE,{"derivedFrom":sQuery(id+"F23.wireOp",EDGE,"E91")}),-1.0]])]});
            extrude(context, id + "F25", {"entities" : qUnion([Q0]), "operationType" : NewBodyOperationType.ADD, "oppositeDirection" : true, "depth" : 5 * mm, "offsetDistance" : 25 * mm});
        }
        {
            var Q0;
            Q0=makeQuery(id+"F17.opExtrude","CAP_EDGE",EDGE,{"disambiguationData":[OSD([sQuery(id+"F16.wireOp",EDGE,"E80")])],"isStart":false});
            var Q1;
            Q1=makeQuery(id+"F17.opExtrude","CAP_EDGE",EDGE,{"disambiguationData":[OSD([sQuery(id+"F16.wireOp",EDGE,"E80")])],"isStart":true});
            fillet(context, id + "F26", {"entities" : qUnion([Q0, Q1]), "radius" : 2 * mm, "tangentPropagation" : true, "allowEdgeOverflow" : false});
        }
        {
            var Q0;
            Q0=makeQuery(id+"F5.imprint","IMPRINT",FACE,{"disambiguationData":[TD([[makeQuery(id+"F5.imprint","IMPRINT",EDGE,{"derivedFrom":sQuery(id+"F5.wireOp",EDGE,"E69.MirrorCS")}),1.0]])]});
            extrude(context, id + "F27", {"entities" : qUnion([Q0]), "operationType" : NewBodyOperationType.REMOVE, "oppositeDirection" : true, "depth" : 9 * mm, "offsetDistance" : 25 * mm});
        }
    });
